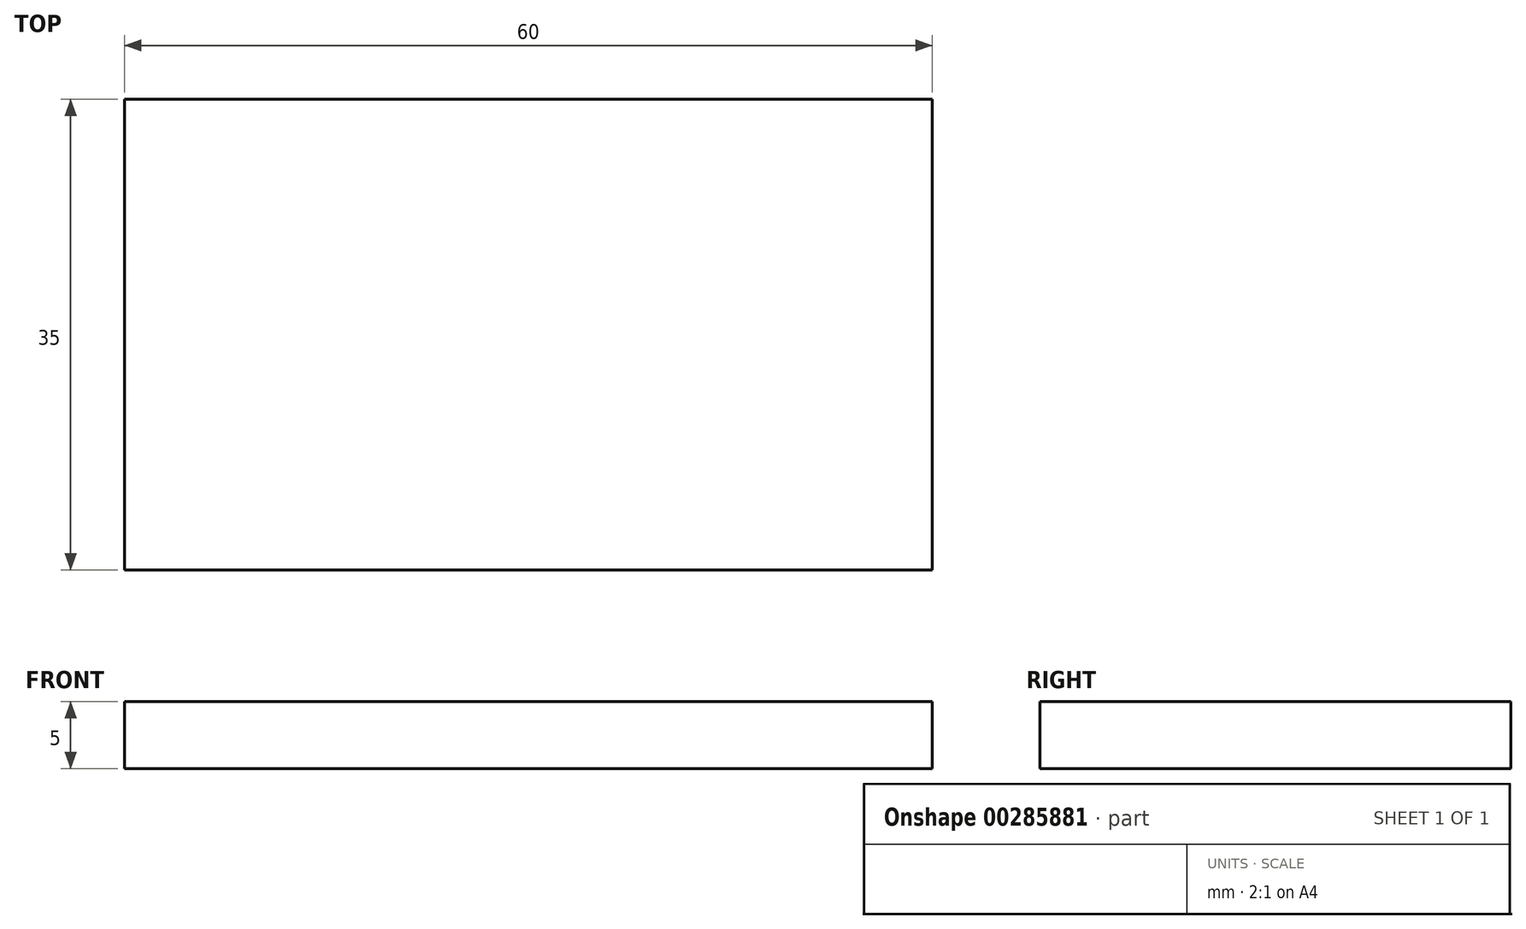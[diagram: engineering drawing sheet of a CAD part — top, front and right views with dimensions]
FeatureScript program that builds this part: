
annotation { "Feature Type Name" : "Feature", "Feature Type Description" : "" }
export const myFeature = defineFeature(function(context is Context, id is Id, definition is map)
    precondition{}
    {
        {
            var Q0;
            Q0=qCreatedBy(makeId("Top.planeOp"),FACE);
            var sketch = newSketch(context, id + "F0", { "sketchPlane" : qUnion([Q0])});
            skLineSegment(sketch, "E0.bottom", {"start": v(-29.74, 16.77) * mm, "end": v(30.26, 16.77) * mm});
            skLineSegment(sketch, "E0.top", {"start": v(-29.74, -18.23) * mm, "end": v(30.26, -18.23) * mm});
            skLineSegment(sketch, "E0.left", {"start": v(-29.74, 16.77) * mm, "end": v(-29.74, -18.23) * mm});
            skLineSegment(sketch, "E0.right", {"start": v(30.26, 16.77) * mm, "end": v(30.26, -18.23) * mm});
            skSolve(sketch);
        }
        {
            var Q0;
            Q0=makeQuery(id+"F0.imprint","IMPRINT",FACE,{"disambiguationData":[TD([[makeQuery(id+"F0.imprint","IMPRINT",EDGE,{"derivedFrom":sQuery(id+"F0.wireOp",EDGE,"E0.bottom")}),-1.0]])]});
            extrude(context, id + "F1", {"entities" : qUnion([Q0]), "depth" : 5 * mm});
        }
    });
